# Revit family: Cable_Tray_Fitting-Solid_Tray-OBO_Bettermann-Channel_Horizontal_Cross_Over-MKS_Magic
name_source: partatom
category: Cable Tray Fittings
revit_build: Autodesk Revit MEP 2012 (Build: 20110309_2315(x64)
units: mm (PartAtom-declared; Revit-internal decimal feet)

## types (2) — shared parameters
Assembly Code = D5030600
Classification = Refer to online Catalog for UL and cUL classifed sizes and wire sizes.
Connector Description = Connector for Cable Tray 1
Connector Description 2 = Connector for Cable Tray 2
Connector Description 3 = Connector for Cable Tray 3
Connector Description 4 = Connector for Cable Tray 4
Description = Solid Cable tray
Manufacturer = OBO Bettermann
Model = MKS-Magic
Pre Galvanized = Yes
Product Page URL = http://catalog2.obo-bettermann.com
Radius = 25  [stored 0.082021 ft]
URL = http://www.obo-bettermann.com

## per-type parameters (varying)
| type | Cable Tray Material |
| Stripped Galvanised | Metal - OBO Bettermann - Strip-Galvanised |
| Hot Dipped Galvanised | Metal - OBO Bettermann - Hot-Dipped-Galvanised |

note: [stored X ft] marks values corroborated as IEEE doubles in the binary element streams (Revit-internal decimal feet)

## geometry (parser evidence)
native form markers: Blend x3, Sweep x4
no freeform markers — native parametric forms only
